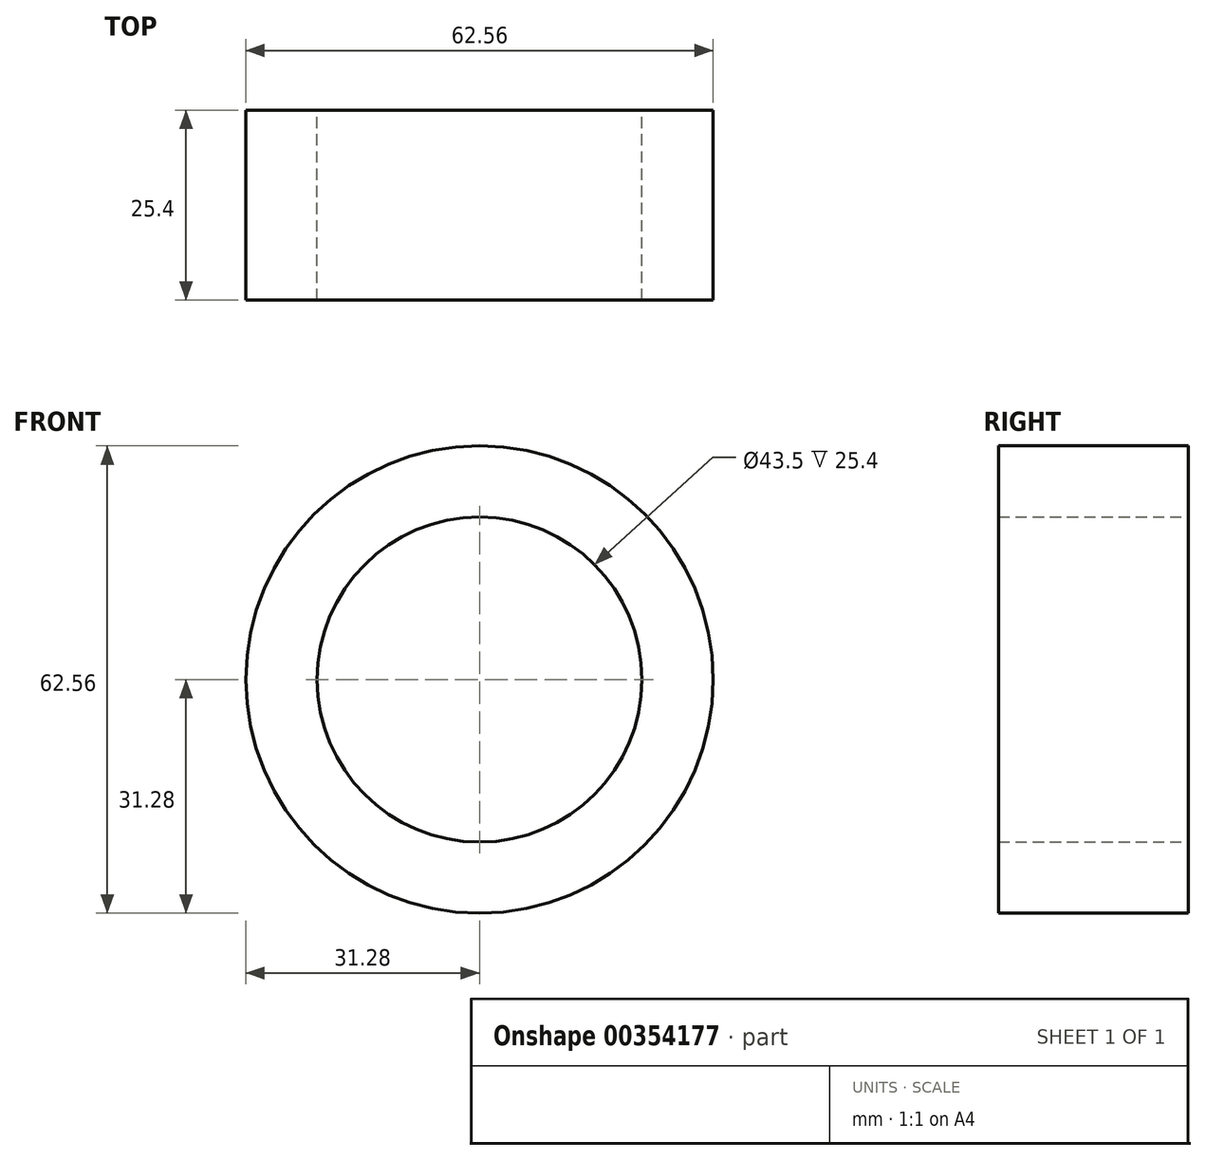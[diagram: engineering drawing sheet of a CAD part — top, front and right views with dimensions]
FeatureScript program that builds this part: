
annotation { "Feature Type Name" : "Feature", "Feature Type Description" : "" }
export const myFeature = defineFeature(function(context is Context, id is Id, definition is map)
    precondition{}
    {
        {
            var Q0;
            Q0=qCreatedBy(makeId("Front.planeOp"),FACE);
            var sketch = newSketch(context, id + "F0", { "sketchPlane" : qUnion([Q0])});
            skCircle(sketch, "E0", {"center": v(0, 0) * mm, "radius": 31.28 * mm});
            skCircle(sketch, "E1", {"center": v(0, 0) * mm, "radius": 21.75 * mm});
            skSolve(sketch);
        }
        {
            var Q0;
            Q0 = qSketchRegion(id + "F0", true);
            extrude(context, id + "F1", {"entities" : qUnion([Q0]), "depth" : 25.4 * mm});
        }
    });
